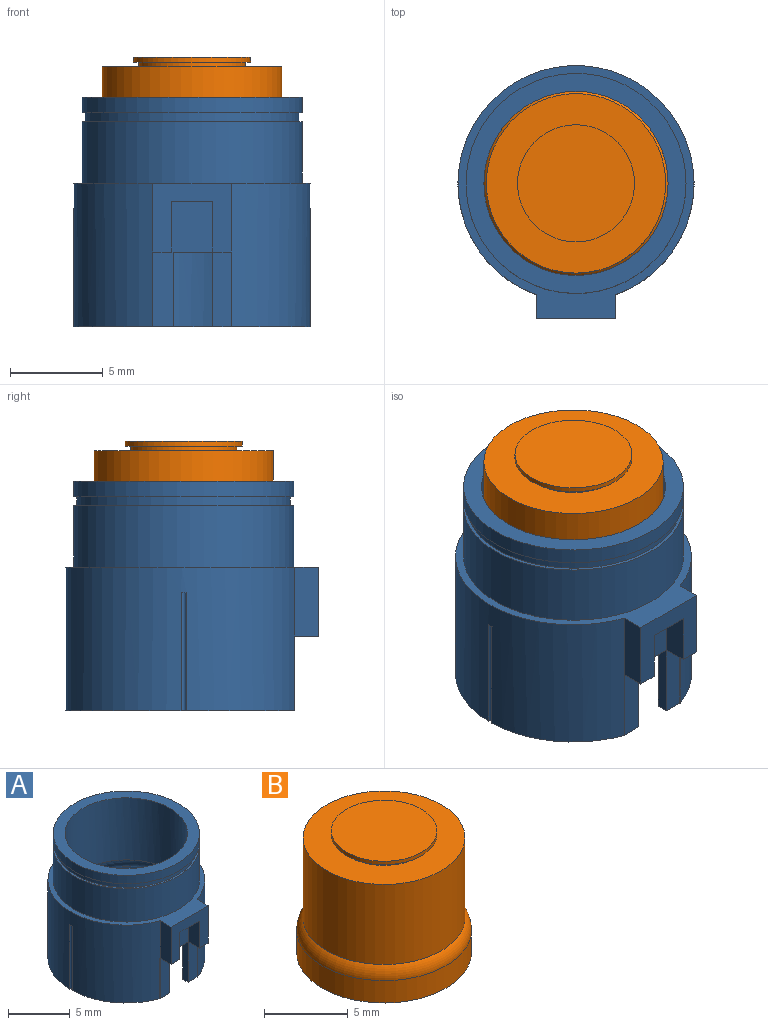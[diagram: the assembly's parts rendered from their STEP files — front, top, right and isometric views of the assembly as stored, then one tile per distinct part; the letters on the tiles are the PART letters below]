
ASSEMBLY  parts=2 mates=1
PART A: 31 faces, bbox 13.5x14x12.3 mm
  f0: plane 6.71x3.23mm, normal (0,-1,0), area 10.5mm2, adj f3,f9,f11,f12,f14,f15,f29,f30
  f1: cylinder r=5.46mm len=10.92mm, axis (0,0,-1), area 169.3mm2, adj f3,f27,f28,f29,f30
  f2: cylinder r=5.92mm len=11.84mm, axis (0,0,-1), area 122.8mm2, adj f8,f25
  f3: plane 12.7x12.34mm, normal (0,0,-1), area 30.7mm2, adj f0,f1,f6,f9,f10,f16,f18,f20
  f4: plane 4.24x3.71mm, normal (0,-1,0), area 9.8mm2, adj f5,f7,f8,f11,f12,f13,f14,f15
  f5: plane 3.71x1.25mm, normal (1,0,0), area 4.6mm2, adj f4,f6,f8,f13
  f6: cylinder r=6.35mm len=12.7mm, axis (0,0,-1), area 271.1mm2, adj f3,f5,f7,f8,f9,f10,f17,f18
  f7: plane 3.71x1.25mm, normal (-1,0,0), area 4.6mm2, adj f4,f6,f8,f12
  f8: plane 13.59x12.7mm, normal (0,0,1), area 20.9mm2, adj f2,f4,f5,f6,f7
  f9: plane 4.01x0.02mm, normal (1,0,0), area 0.1mm2, adj f0,f3,f6,f12
  f10: plane 4.01x0.02mm, normal (-1,0,0), area 0.1mm2, adj f3,f6,f13,f16
  f11: plane 2.69x1.27mm, normal (1,0,0), area 3.4mm2, adj f0,f4,f12,f15
  f12: plane 1.27x1.02mm, normal (0,0,-1), area 1.3mm2, adj f0,f4,f7,f9,f11
  f13: plane 1.27x1.02mm, normal (0,0,-1), area 1.3mm2, adj f4,f5,f10,f14,f16
  f14: plane 2.69x1.27mm, normal (-1,0,0), area 3.4mm2, adj f0,f4,f13,f15
  f15: plane 2.21x1.27mm, normal (0,0,-1), area 2.8mm2, adj f0,f4,f11,f14
  f16: plane 4.01x1.02mm, normal (0,-1,0), area 4.1mm2, adj f3,f10,f13,f28
  f17: plane 0.28x0.14mm, normal (0,0,-1), area 0mm2, adj f6,f18
  f18: cylinder r=0.14mm len=6.35mm, axis (0,0,-1), area 2.8mm2, adj f3,f6,f17
  f19: plane 0.28x0.14mm, normal (0,0,-1), area 0mm2, adj f6,f20
  f20: cylinder r=0.14mm len=6.35mm, axis (0,0,-1), area 2.8mm2, adj f3,f6,f19
  f21: cylinder r=5.92mm len=11.84mm, axis (0,0,-1), area 31.2mm2, adj f23,f26
  f22: cylinder r=4.95mm len=9.91mm, axis (0,0,-1), area 191.3mm2, adj f23,f27
  f23: plane 11.84x11.84mm, normal (0,0,1), area 33mm2, adj f21,f22
  f24: cylinder r=5.74mm len=11.48mm, axis (0,0,1), area 17.4mm2, adj f25,f26
  f25: plane 11.84x11.84mm, normal (0,0,1), area 6.5mm2, adj f2,f24
  f26: plane 11.84x11.84mm, normal (0,0,-1), area 6.5mm2, adj f21,f24
  f27: torus R=6.22mm, axis (0,0,-1), area 37.9mm2, adj f1,f22
  f28: plane 4.01x0.62mm, normal (-1,0,0), area 2.5mm2, adj f1,f3,f16,f29
  f29: plane 2.09x0.62mm, normal (0,0,-1), area 1.1mm2, adj f0,f1,f28,f30
  f30: plane 4.01x0.6mm, normal (1,0,0), area 2.4mm2, adj f0,f1,f3,f29
PART B: 9 faces, bbox 11.3x11.3x8.9 mm
  f0: cylinder r=5.21mm len=10.41mm, axis (0,0,-1), area 53.4mm2, adj f1,f4
  f1: plane 10.41x10.41mm, normal (0,0,-1), area 85.2mm2, adj f0
  f2: cylinder r=4.83mm len=9.65mm, axis (0,0,-1), area 177.1mm2, adj f3,f4
  f3: plane 9.65x9.65mm, normal (0,0,1), area 47.5mm2, adj f2,f5
  f4: torus R=3.94mm, axis (0,0,1), area 32.2mm2, adj f0,f2
  f5: cylinder r=2.86mm len=5.72mm, axis (0,0,-1), area 4.6mm2, adj f3,f8
  f6: cylinder r=3.15mm len=6.3mm, axis (0,0,-1), area 5mm2, adj f7,f8
  f7: plane 6.3x6.3mm, normal (0,0,1), area 31.2mm2, adj f6
  f8: plane 6.3x6.3mm, normal (0,0,-1), area 5.5mm2, adj f5,f6
PLACE A t=(-6.24,-2.99,-5.97)mm fixed
PLACE B rot(axis=(0,0,-1),90deg) t=(-6.24,-2.99,-0.37)mm
MATE slider B.f2 <-> A.f1  axis (0,0,-1) through (-6.24,-2.99,2.17)mm
